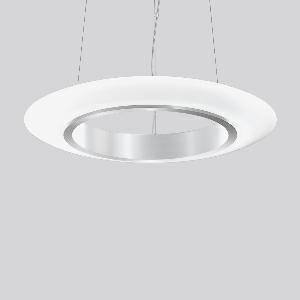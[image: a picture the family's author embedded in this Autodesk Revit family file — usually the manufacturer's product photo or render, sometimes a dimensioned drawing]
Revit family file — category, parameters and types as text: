
# Revit family: ring_of_fire_p_312546_004_1_76_1716
name_source: partatom
category: Lighting Fixtures
units: mm (PartAtom-declared; Revit-internal decimal feet)

## family parameters
Cut with Voids When Loaded = No
Host = Face
Light Source = No
Part Type = Normal
Room Calculation Point = No
Round Connector Dimension = Use Diameter
Shared = No

## types (1)
- RING OF FIRE P (1 x LED Modul 840, 5800 lm, 4000)
    Apparent Load = 71 VA
    CIE Flux Codes = 43 72 90 52 100
    Color Rendering = 80
    Color Temperature = 4000
    Default Elevation = 1800 mm
    Description = Series: RING OF FIRE
A uniquely shaped pendant luminaire with elliptical glass. Supporting ring made of anodised aluminium. Canopy aluminium anodised. Opal glass: mouth-blown, satin finish. Suitable for pendant. 3-point steel cable suspension, steplessly adjustable. Special lengths available on request. 
Colour: anodised aluminium
Diameter: 690 mm
Height: 81 mm
Suspension length: 500-1200 mm
Lamp: LED
Socket: without socket
Colour temperature: 4000K
Colour rendering index (CRI): 80
System power: 71 W
Rated luminous flux: 5800 lm
Luminous efficiency: 82 lm/W
Control gear: Converter, dimmable, DALI
Protection class: I
Type of protection: IP 20
    Height = 81 mm
    Lamp = 1 x LED Modul 840
    Lamp Light Flux = 5800 lm
    Lamp count = 1
    Length = 690 mm
    Lifetime = 50000 h
    Luminous efficacy = 82 lm/W
    Manufacturer = RZB
    ModVariant = No
    Model = 312546.004.1.76
    Mounting Place = Ceiling
    Mounting Type = Pendant
    Number of Poles = 1
    OnlyDefault = Yes
    Power Factor = 1
    Product Name = RING OF FIRE P
    Product group = Pendant luminaires
    ProductGroupID = 902
    Protection Class = Protection class I
    Protection Degree = IP 20
    RLX_Detail_Level = 1
    RLX_Emergency_Light_Flux = 0 lm
    RLX_Emergency_Type = 0
    RLX_Emergency_Type_DB = No
    RlxData = <blob elided: 30341 chars, md5=8b36d16d>
    Socket = socket
    Standby Power = 0 W
    System Light Flux = 5800 lm
    System Power = 71 W
    Type Comments = Product without accessories
    Type Image = 311570.004.jpg
    URL = http://relux.com
    VarID = ---
    Voltage = 230 V
    Voltage Range = 220-240 V
    Weight = 0.00 kg
    Width = 0 mm  [stored 0 ft]

note: [stored X ft] marks values corroborated as IEEE doubles in the binary element streams (Revit-internal decimal feet)

## geometry (parser evidence)
native form markers: Blend x4, Sweep x11
no freeform markers — native parametric forms only
